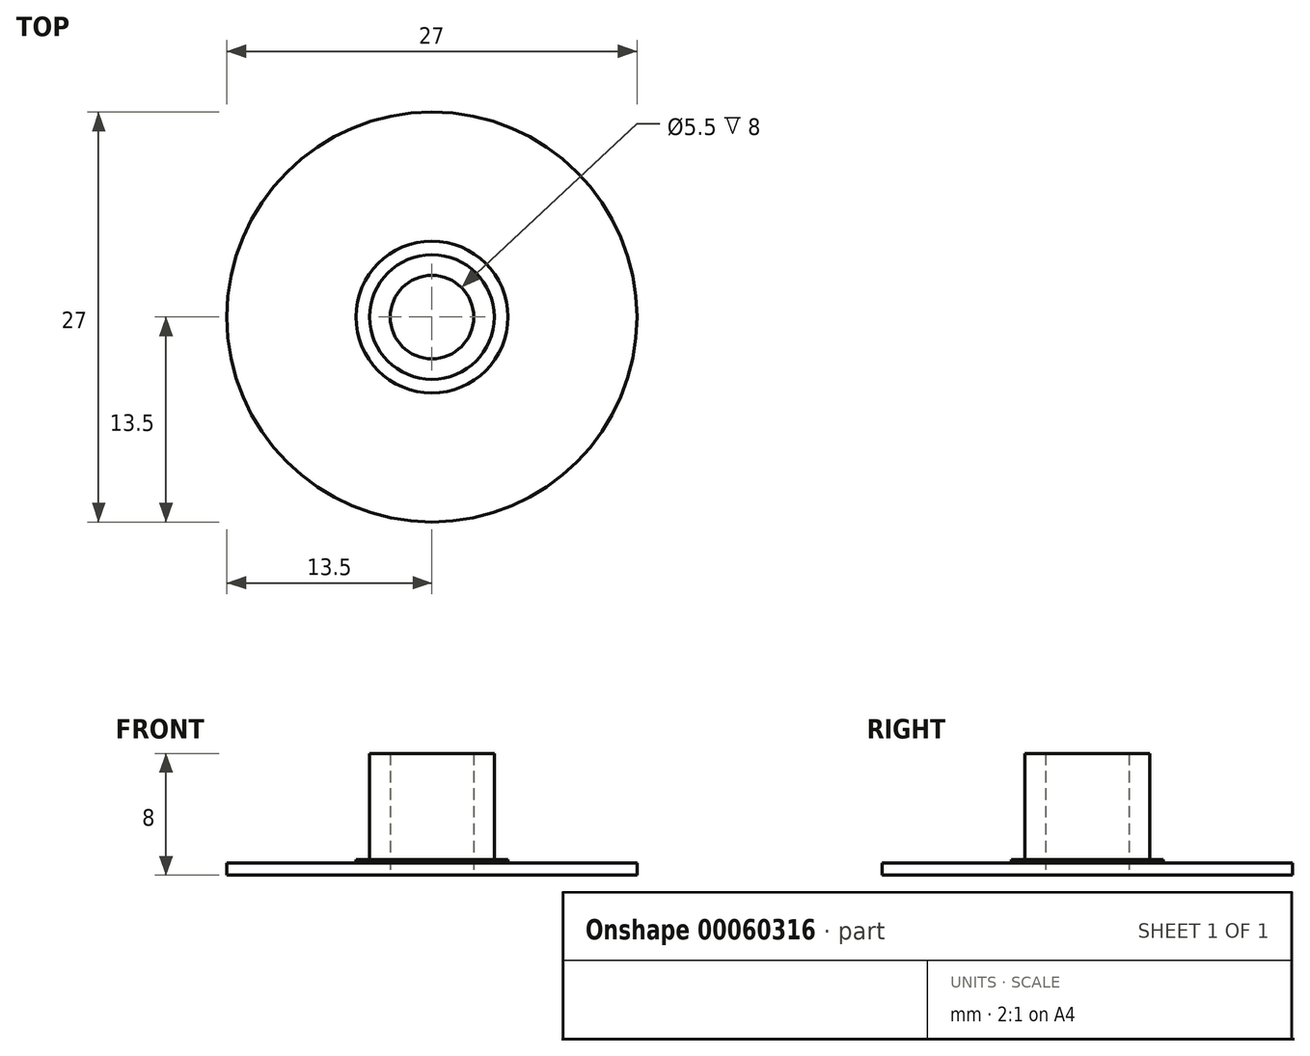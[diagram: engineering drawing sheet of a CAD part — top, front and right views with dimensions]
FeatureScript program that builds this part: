
annotation { "Feature Type Name" : "Feature", "Feature Type Description" : "" }
export const myFeature = defineFeature(function(context is Context, id is Id, definition is map)
    precondition{}
    {
        {
            var Q0;
            Q0=qCreatedBy(makeId("Top.planeOp"),FACE);
            var sketch = newSketch(context, id + "F0", { "sketchPlane" : qUnion([Q0])});
            skCircle(sketch, "E0", {"center": v(0, 0) * mm, "radius": 13.5 * mm});
            skCircle(sketch, "E1", {"center": v(0, 0) * mm, "radius": 2.75 * mm});
            skCircle(sketch, "E2", {"center": v(0, 0) * mm, "radius": 5 * mm});
            skCircle(sketch, "E3", {"center": v(0, 0) * mm, "radius": 4.1 * mm});
            skSolve(sketch);
        }
        {
            var Q0;
            Q0 = qSketchRegion(id + "F0", true);
            extrude(context, id + "F1", {"entities" : qUnion([Q0]), "depth" : 0.8 * mm});
        }
        {
            var Q0;
            Q0=makeQuery(id+"F0.imprint","IMPRINT",FACE,{"disambiguationData":[TD([[makeQuery(id+"F0.imprint","IMPRINT",EDGE,{"derivedFrom":sQuery(id+"F0.wireOp",EDGE,"E1")}),-1.0]])]});
            extrude(context, id + "F2", {"entities" : qUnion([Q0]), "operationType" : NewBodyOperationType.ADD, "depth" : 8 * mm});
        }
        {
            var Q0;
            Q0=makeQuery(id+"F0.imprint","IMPRINT",FACE,{"disambiguationData":[TD([[makeQuery(id+"F0.imprint","IMPRINT",EDGE,{"derivedFrom":sQuery(id+"F0.wireOp",EDGE,"E2")}),1.0]])]});
            extrude(context, id + "F3", {"entities" : qUnion([Q0]), "operationType" : NewBodyOperationType.ADD, "depth" : 1 * mm});
        }
    });
